# Revit family: LAMP_KOMBIC 100 SQUARE IP40 TW OPAL
name_source: partatom
category: Luminarias
revit_build: Autodesk Revit 2018 (Build: 20190510_1515(x64)
units: mm (PartAtom-declared; Revit-internal decimal feet)

## family parameters
Anfitrión = Cara
Compartido = No
Corte con vacíos al cargar = No
Cota de conector redondo = Diámetro de uso
Origen de luz = Sí
Punto de cálculo de habitación = No
Tipo de pieza = Normal

## types (3) — shared parameters
CRI = 90
Cambio de temperatura de color de luz atenuada = <Ninguno>
Dimensions = 99x99x75
Elevación por defecto = 1219 mm
Fabricante = LAMP
Filtro de color = 16777215
Gear = Electronic
Height = 75 mm
IEE = A
Initial color = 2700-5000
Installation instructions = https://www.lamp.es
Insulation class = II
LED Lifetime = 70.000 L80 B10
Lamp = HIGH POWER LED
Last update = 13/07/2021
Luminaire type = Downlight
MacAdam = 3
Manufacturer URL = http://www.lamp.es
Manufacturer country = Spain
Manufacturer name = LAMP
Material aro = LAMP_Plástico genérico BL
Material difusor = LAMP_PMMA Difusor Kombic
Material disipador = LAMP_Aluminio Disipador Kombic
Plum = 21 W
Power = 16 W
Power Supply = 220-240V 50/60Hz
Product URL = https://www.lamp.es
Product datasheet = http://www.lamp.es
Protection rating = IP40
Recessed dimensions = 95x95
Type = BRIDGELUX
Weight = 0.55 kg
Ángulo de inclinación = -90.00°

## per-type parameters (varying)
| type | Archivo de red fotométrica | Efficacy | Finish | Material reflector | Modelo | Product code |
| 1287LM TW DALI W/W | K11SQ2040OP9TWDMW.IES | 62 lm/W | Shiny white RAL 9010 | LAMP_PC Reflector Kombic Metalizado Mate | K11SQ2040OP9TWDMW | K11SQ2040OP9TWDMW |
| 1288LM TW DALI M/W | K11SQ2040OP9TWDWW.IES | 62 lm/W | Matte white RAL 9010 | LAMP_PC Reflector Kombic Blanco | K11SQ2040OP9TWDWW | K11SQ2040OP9TWDWW |
| 1335LM TW DALI BR/W | K11SQ2040OP9TWDRW.IES | 65 lm/W | Shiny white RAL 9010 | LAMP_PC Reflector Kombic Metalizado Brillante | K11SQ2040OP9TWDRW | K11SQ2040OP9TWDRW |
